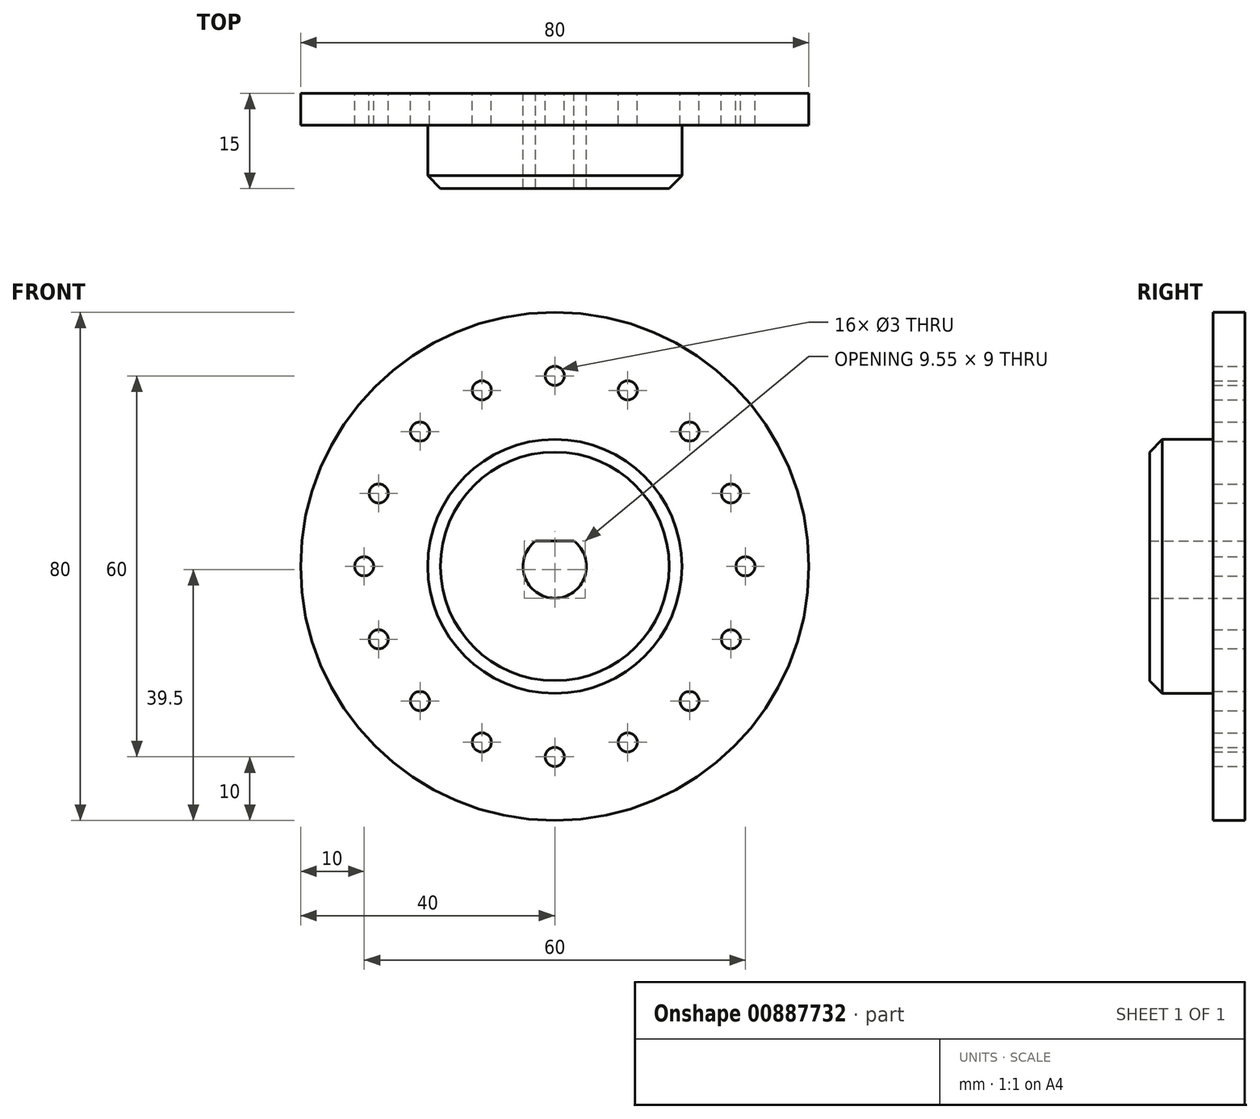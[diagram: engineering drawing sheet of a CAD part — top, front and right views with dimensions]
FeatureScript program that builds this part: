
annotation { "Feature Type Name" : "Feature", "Feature Type Description" : "" }
export const myFeature = defineFeature(function(context is Context, id is Id, definition is map)
    precondition{}
    {
        {
            var Q0;
            Q0=qCreatedBy(makeId("Front.planeOp"),FACE);
            var sketch = newSketch(context, id + "F0", { "sketchPlane" : qUnion([Q0])});
            skCircle(sketch, "E0", {"center": v(0, 0) * mm, "radius": 40 * mm});
            skCircle(sketch, "E1", {"center": v(0, 30) * mm, "radius": 1.5 * mm});
            skCircle(sketch, "E2.1.0", {"center": v(-11.48, 27.72) * mm, "radius": 1.5 * mm});
            skCircle(sketch, "E2.2.0", {"center": v(-21.21, 21.21) * mm, "radius": 1.5 * mm});
            skCircle(sketch, "E2.3.0", {"center": v(-27.72, 11.48) * mm, "radius": 1.5 * mm});
            skCircle(sketch, "E2.4.0", {"center": v(-30, 0) * mm, "radius": 1.5 * mm});
            skCircle(sketch, "E2.5.0", {"center": v(-27.72, -11.48) * mm, "radius": 1.5 * mm});
            skCircle(sketch, "E2.6.0", {"center": v(-21.21, -21.21) * mm, "radius": 1.5 * mm});
            skCircle(sketch, "E2.7.0", {"center": v(-11.48, -27.72) * mm, "radius": 1.5 * mm});
            skCircle(sketch, "E2.8.0", {"center": v(0, -30) * mm, "radius": 1.5 * mm});
            skCircle(sketch, "E2.9.0", {"center": v(11.48, -27.72) * mm, "radius": 1.5 * mm});
            skCircle(sketch, "E2.10.0", {"center": v(21.21, -21.21) * mm, "radius": 1.5 * mm});
            skCircle(sketch, "E2.11.0", {"center": v(27.72, -11.48) * mm, "radius": 1.5 * mm});
            skCircle(sketch, "E2.12.0", {"center": v(30, 0) * mm, "radius": 1.5 * mm});
            skCircle(sketch, "E2.13.0", {"center": v(27.72, 11.48) * mm, "radius": 1.5 * mm});
            skCircle(sketch, "E2.14.0", {"center": v(21.21, 21.21) * mm, "radius": 1.5 * mm});
            skCircle(sketch, "E2.15.0", {"center": v(11.48, 27.72) * mm, "radius": 1.5 * mm});
            skSolve(sketch);
        }
        {
            var Q0;
            Q0 = qSketchRegion(id + "F0", true);
            extrude(context, id + "F1", {"entities" : qUnion([Q0]), "depth" : 5 * mm, "offsetDistance" : 25 * mm});
        }
        {
            var Q0;
            Q0=makeQuery(id+"F1.opExtrude","CAP_FACE",FACE,{"disambiguationData":[OSD([sQuery(id+"F0.wireOp",EDGE,"E0"),sQuery(id+"F0.wireOp",EDGE,"E1"),sQuery(id+"F0.wireOp",EDGE,"E2.1.0"),sQuery(id+"F0.wireOp",EDGE,"E2.2.0"),sQuery(id+"F0.wireOp",EDGE,"E2.3.0"),sQuery(id+"F0.wireOp",EDGE,"E2.4.0"),sQuery(id+"F0.wireOp",EDGE,"E2.5.0"),sQuery(id+"F0.wireOp",EDGE,"E2.6.0"),sQuery(id+"F0.wireOp",EDGE,"E2.7.0"),sQuery(id+"F0.wireOp",EDGE,"E2.8.0"),sQuery(id+"F0.wireOp",EDGE,"E2.9.0"),sQuery(id+"F0.wireOp",EDGE,"E2.10.0"),sQuery(id+"F0.wireOp",EDGE,"E2.11.0"),sQuery(id+"F0.wireOp",EDGE,"E2.12.0"),sQuery(id+"F0.wireOp",EDGE,"E2.13.0"),sQuery(id+"F0.wireOp",EDGE,"E2.14.0"),sQuery(id+"F0.wireOp",EDGE,"E2.15.0")])],"isStart":false});
            var sketch = newSketch(context, id + "F2", { "sketchPlane" : qUnion([Q0])});
            skArc(sketch, "E3", {"start": v(-3, 4) * mm, "mid": v(0, -5) * mm, "end": v(3, 4) * mm});
            skLineSegment(sketch, "E4", {"start": v(-3, 4) * mm, "end": v(3, 4) * mm});
            skCircle(sketch, "E5", {"center": v(0, 0) * mm, "radius": 20 * mm});
            skSolve(sketch);
        }
        {
            var Q0;
            Q0=makeQuery(id+"F2.imprint","IMPRINT",FACE,{"disambiguationData":[TD([[makeQuery(id+"F2.imprint","IMPRINT",EDGE,{"derivedFrom":sQuery(id+"F2.wireOp",EDGE,"E3")}),-1.0]])]});
            extrude(context, id + "F3", {"entities" : qUnion([Q0]), "operationType" : NewBodyOperationType.ADD, "depth" : 10 * mm, "offsetDistance" : 25 * mm});
        }
        {
            var Q0;
            Q0=makeQuery(id+"F3.boolean.opBoolean","SPLIT",FACE,{"disambiguationData":[TD([makeQuery(id+"F3.opExtrude","SWEPT_FACE",FACE,{"disambiguationData":[OSD([sQuery(id+"F2.wireOp",EDGE,"E3")])]})])],"derivedFrom":makeQuery(id+"F1.opExtrude","CAP_FACE",FACE,{"disambiguationData":[OSD([sQuery(id+"F0.wireOp",EDGE,"E0"),sQuery(id+"F0.wireOp",EDGE,"E1"),sQuery(id+"F0.wireOp",EDGE,"E2.1.0"),sQuery(id+"F0.wireOp",EDGE,"E2.2.0"),sQuery(id+"F0.wireOp",EDGE,"E2.3.0"),sQuery(id+"F0.wireOp",EDGE,"E2.4.0"),sQuery(id+"F0.wireOp",EDGE,"E2.5.0"),sQuery(id+"F0.wireOp",EDGE,"E2.6.0"),sQuery(id+"F0.wireOp",EDGE,"E2.7.0"),sQuery(id+"F0.wireOp",EDGE,"E2.8.0"),sQuery(id+"F0.wireOp",EDGE,"E2.9.0"),sQuery(id+"F0.wireOp",EDGE,"E2.10.0"),sQuery(id+"F0.wireOp",EDGE,"E2.11.0"),sQuery(id+"F0.wireOp",EDGE,"E2.12.0"),sQuery(id+"F0.wireOp",EDGE,"E2.13.0"),sQuery(id+"F0.wireOp",EDGE,"E2.14.0"),sQuery(id+"F0.wireOp",EDGE,"E2.15.0")])],"isStart":false})});
            extrude(context, id + "F4", {"entities" : qUnion([Q0]), "operationType" : NewBodyOperationType.REMOVE, "endBound" : BoundingType.THROUGH_ALL, "oppositeDirection" : true, "depth" : 25 * mm, "offsetDistance" : 25 * mm});
        }
        {
            var Q0;
            Q0=makeQuery(id+"F3.opExtrude","CAP_EDGE",EDGE,{"disambiguationData":[OSD([sQuery(id+"F2.wireOp",EDGE,"E5")])],"isStart":false});
            var Q1;
            Q1=makeQuery(id+"F3.opExtrude","CAP_EDGE",EDGE,{"disambiguationData":[OSD([sQuery(id+"F2.wireOp",EDGE,"E5")])],"isStart":true});
            chamfer(context, id + "F5", {"entities" : qUnion([Q0, Q1]), "width" : 2 * mm, "tangentPropagation" : true});
        }
    });
